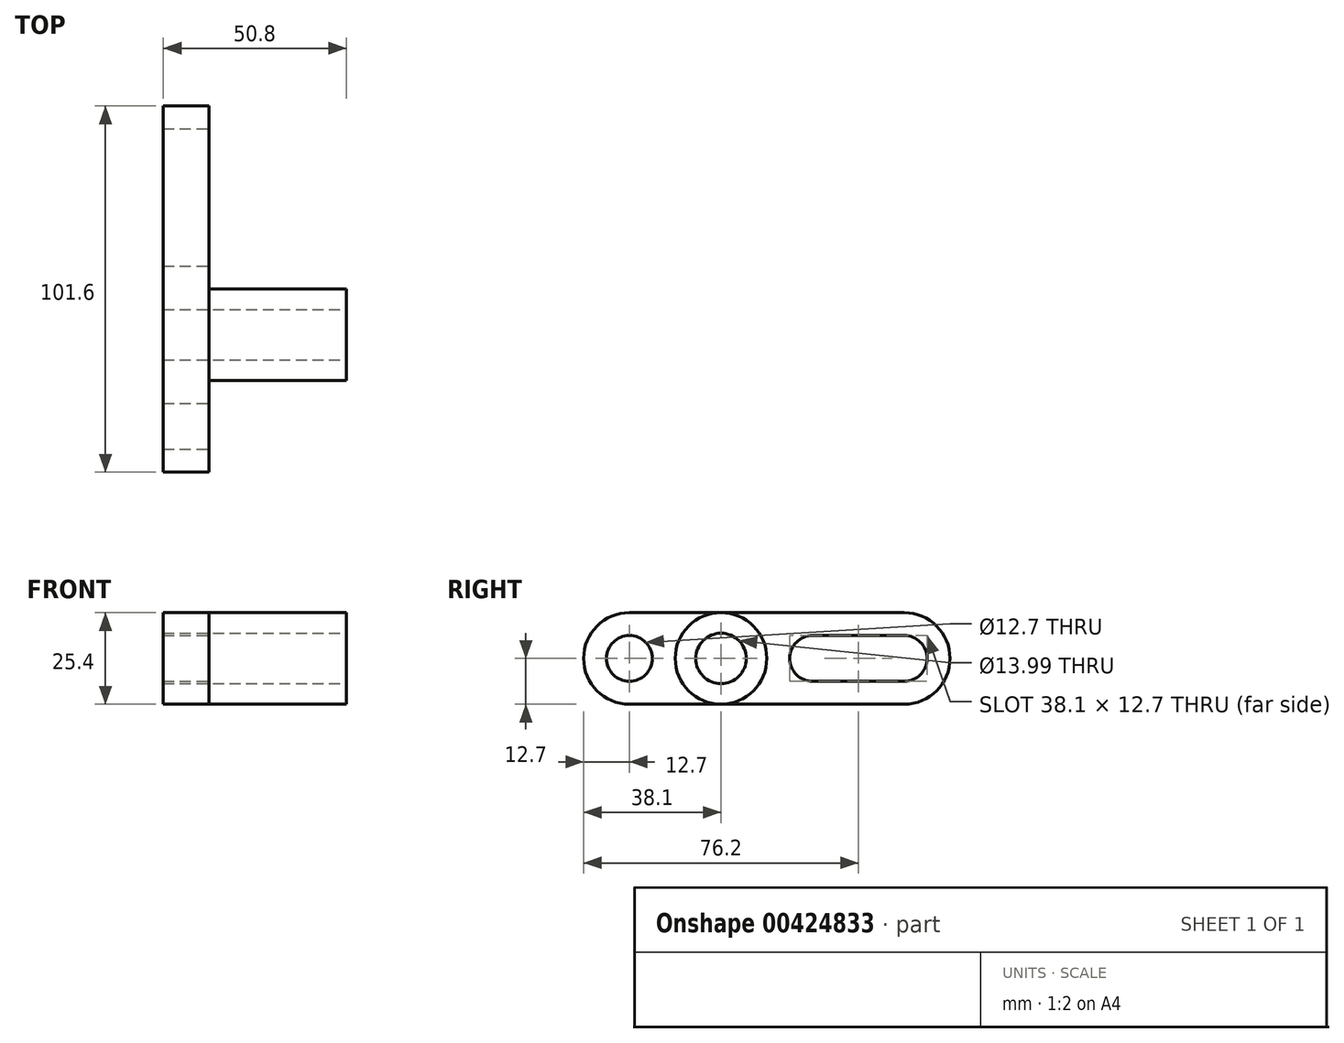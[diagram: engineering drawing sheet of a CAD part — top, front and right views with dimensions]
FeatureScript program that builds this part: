
annotation { "Feature Type Name" : "Feature", "Feature Type Description" : "" }
export const myFeature = defineFeature(function(context is Context, id is Id, definition is map)
    precondition{}
    {
        {
            var Q0;
            Q0=qCreatedBy(makeId("Right.planeOp"),FACE);
            var sketch = newSketch(context, id + "F0", { "sketchPlane" : qUnion([Q0])});
            skLineSegment(sketch, "E0", {"start": v(0, 0) * mm, "end": v(0, 25.4) * mm});
            skLineSegment(sketch, "E1", {"start": v(0, 25.4) * mm, "end": v(101.6, 25.4) * mm});
            skLineSegment(sketch, "E2", {"start": v(101.6, 25.4) * mm, "end": v(101.6, 0) * mm});
            skLineSegment(sketch, "E3", {"start": v(101.6, 0) * mm, "end": v(0, 0) * mm});
            skSolve(sketch);
        }
        {
            var Q0;
            Q0 = qSketchRegion(id + "F0", true);
            extrude(context, id + "F1", {"entities" : qUnion([Q0]), "depth" : 12.7 * mm});
        }
        {
            var Q0;
            Q0=makeQuery(id+"F1.opExtrude","CAP_FACE",FACE,{"disambiguationData":[OSD([sQuery(id+"F0.wireOp",EDGE,"E0"),sQuery(id+"F0.wireOp",EDGE,"E1"),sQuery(id+"F0.wireOp",EDGE,"E2"),sQuery(id+"F0.wireOp",EDGE,"E3")])],"isStart":false});
            var sketch = newSketch(context, id + "F2", { "sketchPlane" : qUnion([Q0])});
            skArc(sketch, "E4", {"start": v(88.9, 0) * mm, "mid": v(101.6, 12.7) * mm, "end": v(88.9, 25.4) * mm});
            skArc(sketch, "E5", {"start": v(12.7, 25.4) * mm, "mid": v(0, 12.7) * mm, "end": v(12.7, 0) * mm});
            skSolve(sketch);
        }
        {
            var Q0;
            {var subQ0=sQuery(id+"F2.wireOp",EDGE,"E5");var subQ1=makeQuery(id+"F1.opExtrude","CAP_EDGE",EDGE,{"disambiguationData":[OSD([sQuery(id+"F0.wireOp",EDGE,"E1")])],"isStart":false});var subQ2=makeQuery(id+"F2.imprint","INTERSECT",VERTEX,{"derivedFrom":[subQ1,subQ0]});Q0=makeQuery(id+"F2.imprint","IMPRINT",FACE,{"disambiguationData":[TD([[makeQuery(id+"F2.imprint","IMPRINT",EDGE,{"disambiguationData":[TD([[subQ2,-1.0]])],"derivedFrom":subQ0}),-1.0]])]});}
            var Q1;
            {var subQ0=sQuery(id+"F2.wireOp",EDGE,"E5");var subQ1=makeQuery(id+"F1.opExtrude","CAP_EDGE",EDGE,{"disambiguationData":[OSD([sQuery(id+"F0.wireOp",EDGE,"E3")])],"isStart":false});var subQ2=makeQuery(id+"F2.imprint","INTERSECT",VERTEX,{"derivedFrom":[subQ1,subQ0]});Q1=makeQuery(id+"F2.imprint","IMPRINT",FACE,{"disambiguationData":[TD([[makeQuery(id+"F2.imprint","IMPRINT",EDGE,{"disambiguationData":[TD([[subQ2,1.0]])],"derivedFrom":subQ0}),-1.0]])]});}
            var Q2;
            {var subQ0=sQuery(id+"F2.wireOp",EDGE,"E4");var subQ1=makeQuery(id+"F1.opExtrude","CAP_EDGE",EDGE,{"disambiguationData":[OSD([sQuery(id+"F0.wireOp",EDGE,"E2")])],"isStart":false});var subQ2=makeQuery(id+"F2.imprint","INTERSECT",VERTEX,{"derivedFrom":[subQ1,subQ0]});Q2=makeQuery(id+"F2.imprint","IMPRINT",FACE,{"disambiguationData":[TD([[makeQuery(id+"F2.imprint","IMPRINT",EDGE,{"disambiguationData":[TD([[subQ2,-1.0]])],"derivedFrom":subQ0}),-1.0]])]});}
            var Q3;
            {var subQ0=sQuery(id+"F2.wireOp",EDGE,"E4");var subQ1=makeQuery(id+"F1.opExtrude","CAP_EDGE",EDGE,{"disambiguationData":[OSD([sQuery(id+"F0.wireOp",EDGE,"E2")])],"isStart":false});var subQ2=makeQuery(id+"F2.imprint","INTERSECT",VERTEX,{"derivedFrom":[subQ1,subQ0]});Q3=makeQuery(id+"F2.imprint","IMPRINT",FACE,{"disambiguationData":[TD([[makeQuery(id+"F2.imprint","IMPRINT",EDGE,{"disambiguationData":[TD([[subQ2,1.0]])],"derivedFrom":subQ0}),-1.0]])]});}
            extrude(context, id + "F3", {"entities" : qUnion([Q0, Q1, Q2, Q3]), "operationType" : NewBodyOperationType.REMOVE, "oppositeDirection" : true, "depth" : 12.7 * mm});
        }
        {
            var Q0;
            Q0=makeQuery(id+"F1.opExtrude","CAP_FACE",FACE,{"disambiguationData":[OSD([sQuery(id+"F0.wireOp",EDGE,"E0"),sQuery(id+"F0.wireOp",EDGE,"E1"),sQuery(id+"F0.wireOp",EDGE,"E2"),sQuery(id+"F0.wireOp",EDGE,"E3")])],"isStart":false});
            var sketch = newSketch(context, id + "F4", { "sketchPlane" : qUnion([Q0])});
            skCircle(sketch, "E6", {"center": v(63.5, 12.7) * mm, "radius": 6.35 * mm});
            skCircle(sketch, "E7", {"center": v(88.9, 12.7) * mm, "radius": 6.35 * mm});
            skCircle(sketch, "E8", {"center": v(12.7, 12.7) * mm, "radius": 6.35 * mm});
            skLineSegment(sketch, "E9", {"start": v(63.5, 19.05) * mm, "end": v(88.9, 19.05) * mm});
            skLineSegment(sketch, "E10", {"start": v(63.5, 6.35) * mm, "end": v(88.9, 6.35) * mm});
            skLineSegment(sketch, "E11", {"start": v(88.9, 6.35) * mm, "end": v(88.9, 12.7) * mm});
            skSolve(sketch);
        }
        {
            var Q0;
            Q0=makeQuery(id+"F4.imprint","IMPRINT",FACE,{"disambiguationData":[TD([[makeQuery(id+"F4.imprint","IMPRINT",EDGE,{"derivedFrom":sQuery(id+"F4.wireOp",EDGE,"E8")}),1.0]])]});
            var Q1;
            {var subQ0=sQuery(id+"F4.wireOp",EDGE,"E6");var subQ1=makeQuery(id+"F4.imprint","INTERSECT",VERTEX,{"derivedFrom":[subQ0,sQuery(id+"F4.wireOp",EDGE,"E9")]});Q1=makeQuery(id+"F4.imprint","IMPRINT",FACE,{"disambiguationData":[TD([[makeQuery(id+"F4.imprint","IMPRINT",EDGE,{"disambiguationData":[TD([[subQ1,-1.0]])],"derivedFrom":subQ0}),1.0]])]});}
            var Q2;
            {var subQ0=sQuery(id+"F4.wireOp",EDGE,"E9");Q2=makeQuery(id+"F4.imprint","IMPRINT",FACE,{"disambiguationData":[TD([[makeQuery(id+"F4.imprint","IMPRINT",EDGE,{"derivedFrom":subQ0}),-1.0]])]});}
            var Q3;
            {var subQ0=sQuery(id+"F4.wireOp",EDGE,"E7");var subQ1=makeQuery(id+"F4.imprint","INTERSECT",VERTEX,{"derivedFrom":[subQ0,sQuery(id+"F4.wireOp",EDGE,"E9")]});Q3=makeQuery(id+"F4.imprint","IMPRINT",FACE,{"disambiguationData":[TD([[makeQuery(id+"F4.imprint","IMPRINT",EDGE,{"disambiguationData":[TD([[subQ1,-1.0]])],"derivedFrom":subQ0}),1.0]])]});}
            extrude(context, id + "F5", {"entities" : qUnion([Q0, Q1, Q2, Q3]), "operationType" : NewBodyOperationType.REMOVE, "oppositeDirection" : true, "depth" : 12.7 * mm});
        }
        {
            var Q0;
            Q0=makeQuery(id+"F1.opExtrude","CAP_FACE",FACE,{"disambiguationData":[OSD([sQuery(id+"F0.wireOp",EDGE,"E0"),sQuery(id+"F0.wireOp",EDGE,"E1"),sQuery(id+"F0.wireOp",EDGE,"E2"),sQuery(id+"F0.wireOp",EDGE,"E3")])],"isStart":false});
            var sketch = newSketch(context, id + "F6", { "sketchPlane" : qUnion([Q0])});
            skSolve(sketch);
        }
        {
            var Q0;
            {var subQ1=makeQuery(id+"F1.opExtrude","CAP_EDGE",EDGE,{"disambiguationData":[OSD([sQuery(id+"F0.wireOp",EDGE,"E1")])],"isStart":false});Q0=makeQuery(id+"F6.imprint","IMPRINT",FACE,{"disambiguationData":[TD([[makeQuery(id+"F6.imprint","IMPRINT",EDGE,{"derivedFrom":subQ1}),-1.0]])]});}
            var sketch = newSketch(context, id + "F7", { "sketchPlane" : qUnion([Q0])});
            skCircle(sketch, "E12", {"center": v(38.1, 12.7) * mm, "radius": 12.7 * mm});
            skSolve(sketch);
        }
        {
            var Q0;
            Q0 = qSketchRegion(id + "F7", true);
            extrude(context, id + "F8", {"entities" : qUnion([Q0]), "operationType" : NewBodyOperationType.ADD, "depth" : 38.1 * mm});
        }
        {
            var Q0;
            Q0=makeQuery(id+"F8.opExtrude","CAP_FACE",FACE,{"disambiguationData":[OSD([sQuery(id+"F7.wireOp",EDGE,"E12")])],"isStart":false});
            var sketch = newSketch(context, id + "F9", { "sketchPlane" : qUnion([Q0])});
            skCircle(sketch, "E13", {"center": v(38.1, 12.7) * mm, "radius": 7 * mm});
            skSolve(sketch);
        }
        {
            var Q0;
            Q0=makeQuery(id+"F9.imprint","IMPRINT",FACE,{"disambiguationData":[TD([[makeQuery(id+"F9.imprint","IMPRINT",EDGE,{"derivedFrom":sQuery(id+"F9.wireOp",EDGE,"E13")}),1.0]])]});
            extrude(context, id + "F10", {"entities" : qUnion([Q0]), "operationType" : NewBodyOperationType.REMOVE, "oppositeDirection" : true, "depth" : 50.8 * mm});
        }
    });
